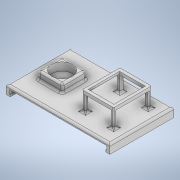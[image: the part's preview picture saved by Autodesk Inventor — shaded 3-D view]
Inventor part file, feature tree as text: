
AUTODESK INVENTOR PART (.ipt)
format: ipt  version: 2020 (Build 240168000, 168)  size: 340,480 bytes
history: native  units: in
note: dims shown in document units (in); Inventor stores cm internally (conversion verified against a paired STEP export)
features: extrude x7, sketch x7, fillet x3
ambient origin geometry x8: Origin, YZ Plane, XZ Plane, XY Plane, X Axis, Y Axis, Z Axis, Center Point
bodies: Solid1 (feature_tree)
feature tree (17):
  extrude  "Extrusion1"  Depth=4.0in
  extrude  "Extrusion2"  Depth=0.25in
  extrude  "Extrusion3"  Depth=0.375in TaperAngle=0.0deg
  extrude  "Extrusion4"  Depth=0.25in
  extrude  "Extrusion5"  Depth=0.25in
  extrude  "Extrusion6"  Depth=1.0in
  fillet  "Fillet1"  Radius=0.7902in
  extrude  "Extrusion7"  Depth=0.0625in
  fillet  "Fillet2"  Radius=0.1969in
  fillet  "Fillet3"  Radius=0.1969in
  sketch  "Sketch1"  dims[d0=6.5in d1=4.0in]
  sketch  "Sketch2"  dims[d2=0.1875in d3=0.0in d4=0.25in]
  sketch  "Sketch3"  dims[d5=0.25in d6=0.375in d7=0.0in]
  sketch  "Sketch4"  dims[d8=0.05in d9=0.25in]
  sketch  "Sketch5"  dims[d10=0.05in d11=0.25in]
  sketch  "Sketch6"  dims[d12=0.0in d13=0.0in d14=1.0in d15=0.7902in]
  sketch  "Sketch7"  dims[d16=1.9685in d17=2.3622in d18=0.1969in d19=0.1969in d20=0.1969in d21=0.1969in d22=0.1969in d23=0.1969in d24=0.1969in d25=0.1969in d26=0.9843in d27=0.0in d28=0.1969in d29=0.0in d30=1.6142in d31=1.9685in d32=0.1969in d33=0.0in d34=0.125in d35=1.5in d36=1.5in d37=1.5in d38=1.3in d39=0.5in d40=0.0in d41=0.125in d42=0.0625in]
